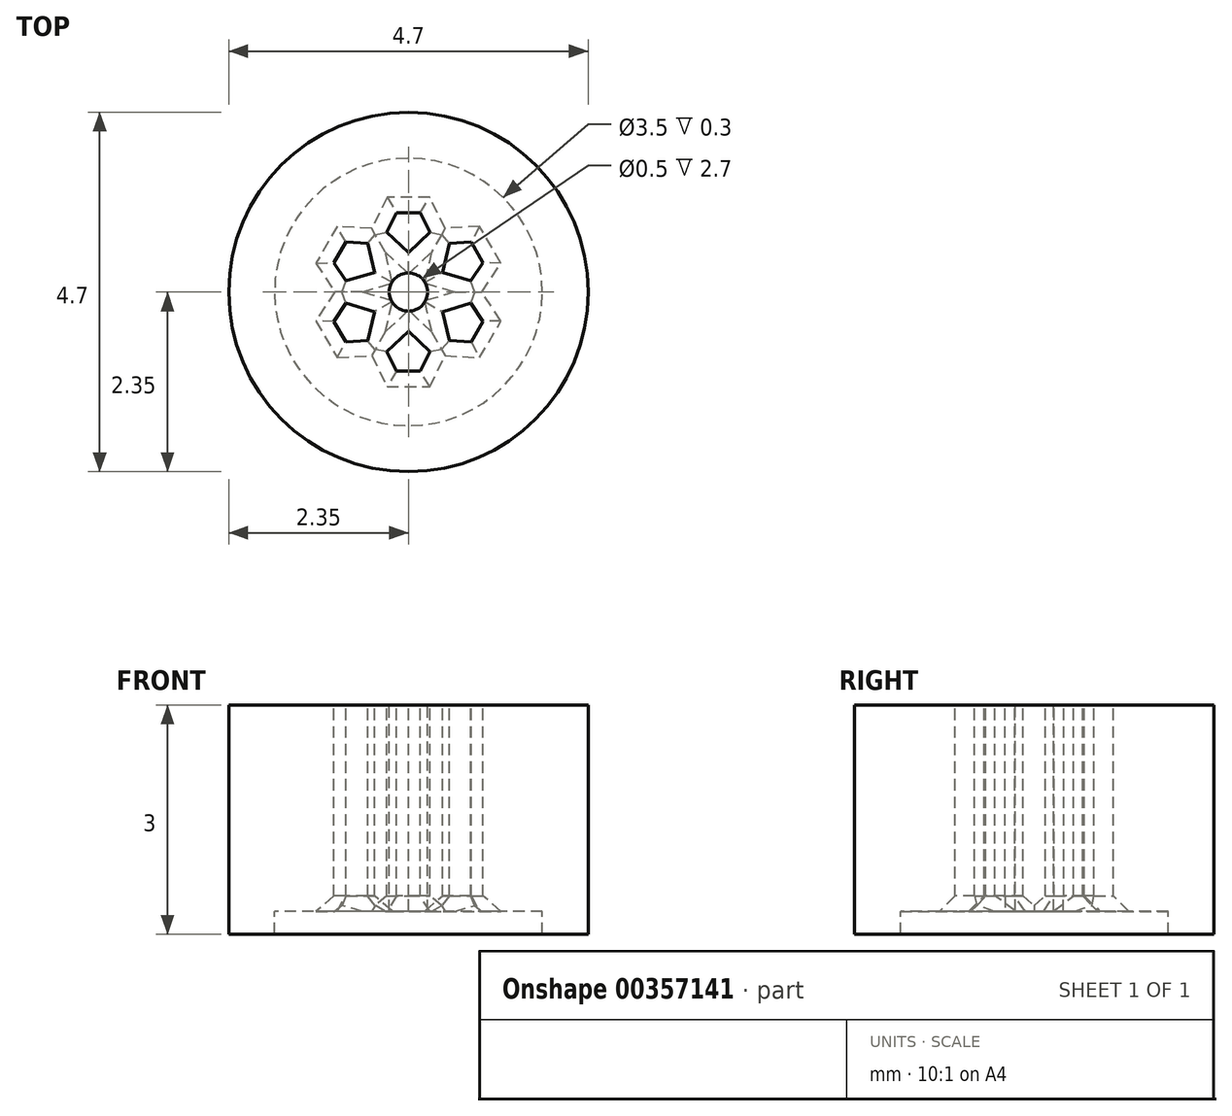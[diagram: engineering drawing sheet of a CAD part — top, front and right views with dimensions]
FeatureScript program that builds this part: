
annotation { "Feature Type Name" : "Feature", "Feature Type Description" : "" }
export const myFeature = defineFeature(function(context is Context, id is Id, definition is map)
    precondition{}
    {
        {
            var Q0;
            Q0=qCreatedBy(makeId("Top.planeOp"),FACE);
            var sketch = newSketch(context, id + "F0", { "sketchPlane" : qUnion([Q0])});
            skCircle(sketch, "E0", {"center": v(0, 0) * mm, "radius": 2.35 * mm});
            skCircle(sketch, "E1", {"center": v(0, 0) * mm, "radius": 1.75 * mm});
            skCircle(sketch, "E2", {"center": v(0, 0) * mm, "radius": 0.25 * mm});
            skLineSegment(sketch, "E3", {"start": v(0, 0.51) * mm, "end": v(0.28, 0.78) * mm});
            skLineSegment(sketch, "E4", {"start": v(0.28, 0.78) * mm, "end": v(0.15, 1.04) * mm});
            skLineSegment(sketch, "E5", {"start": v(0.15, 1.04) * mm, "end": v(0, 1.04) * mm});
            skLineSegment(sketch, "E6.MirrorCS", {"start": v(-0.15, 1.04) * mm, "end": v(0, 1.04) * mm});
            skLineSegment(sketch, "E7.MirrorCS", {"start": v(-0.28, 0.78) * mm, "end": v(-0.15, 1.04) * mm});
            skLineSegment(sketch, "E8.MirrorCS", {"start": v(0, 0.51) * mm, "end": v(-0.28, 0.78) * mm});
            skLineSegment(sketch, "E9.1.0", {"start": v(0.44, 0.26) * mm, "end": v(0.53, 0.63) * mm});
            skLineSegment(sketch, "E9.1.1", {"start": v(0.44, 0.26) * mm, "end": v(0.82, 0.14) * mm});
            skLineSegment(sketch, "E9.1.2", {"start": v(0.82, 0.14) * mm, "end": v(0.97, 0.38) * mm});
            skLineSegment(sketch, "E9.1.3", {"start": v(0.97, 0.38) * mm, "end": v(0.9, 0.52) * mm});
            skLineSegment(sketch, "E9.1.4", {"start": v(0.82, 0.65) * mm, "end": v(0.9, 0.52) * mm});
            skLineSegment(sketch, "E9.1.5", {"start": v(0.53, 0.63) * mm, "end": v(0.82, 0.65) * mm});
            skLineSegment(sketch, "E9.2.0", {"start": v(0.44, -0.26) * mm, "end": v(0.82, -0.14) * mm});
            skLineSegment(sketch, "E9.2.1", {"start": v(0.44, -0.26) * mm, "end": v(0.53, -0.63) * mm});
            skLineSegment(sketch, "E9.2.2", {"start": v(0.53, -0.63) * mm, "end": v(0.82, -0.65) * mm});
            skLineSegment(sketch, "E9.2.3", {"start": v(0.82, -0.65) * mm, "end": v(0.9, -0.52) * mm});
            skLineSegment(sketch, "E9.2.4", {"start": v(0.97, -0.38) * mm, "end": v(0.9, -0.52) * mm});
            skLineSegment(sketch, "E9.2.5", {"start": v(0.82, -0.14) * mm, "end": v(0.97, -0.38) * mm});
            skLineSegment(sketch, "E9.3.0", {"start": v(0, -0.51) * mm, "end": v(0.28, -0.78) * mm});
            skLineSegment(sketch, "E9.3.1", {"start": v(0, -0.51) * mm, "end": v(-0.28, -0.78) * mm});
            skLineSegment(sketch, "E9.3.2", {"start": v(-0.28, -0.78) * mm, "end": v(-0.15, -1.04) * mm});
            skLineSegment(sketch, "E9.3.3", {"start": v(-0.15, -1.04) * mm, "end": v(0, -1.04) * mm});
            skLineSegment(sketch, "E9.3.4", {"start": v(0.15, -1.04) * mm, "end": v(0, -1.04) * mm});
            skLineSegment(sketch, "E9.3.5", {"start": v(0.28, -0.78) * mm, "end": v(0.15, -1.04) * mm});
            skLineSegment(sketch, "E9.4.0", {"start": v(-0.44, -0.26) * mm, "end": v(-0.53, -0.63) * mm});
            skLineSegment(sketch, "E9.4.1", {"start": v(-0.44, -0.26) * mm, "end": v(-0.82, -0.14) * mm});
            skLineSegment(sketch, "E9.4.2", {"start": v(-0.82, -0.14) * mm, "end": v(-0.97, -0.38) * mm});
            skLineSegment(sketch, "E9.4.3", {"start": v(-0.97, -0.38) * mm, "end": v(-0.9, -0.52) * mm});
            skLineSegment(sketch, "E9.4.4", {"start": v(-0.82, -0.65) * mm, "end": v(-0.9, -0.52) * mm});
            skLineSegment(sketch, "E9.4.5", {"start": v(-0.53, -0.63) * mm, "end": v(-0.82, -0.65) * mm});
            skLineSegment(sketch, "E9.5.0", {"start": v(-0.44, 0.26) * mm, "end": v(-0.82, 0.14) * mm});
            skLineSegment(sketch, "E9.5.1", {"start": v(-0.44, 0.26) * mm, "end": v(-0.53, 0.63) * mm});
            skLineSegment(sketch, "E9.5.2", {"start": v(-0.53, 0.63) * mm, "end": v(-0.82, 0.65) * mm});
            skLineSegment(sketch, "E9.5.3", {"start": v(-0.82, 0.65) * mm, "end": v(-0.9, 0.52) * mm});
            skLineSegment(sketch, "E9.5.4", {"start": v(-0.97, 0.38) * mm, "end": v(-0.9, 0.52) * mm});
            skLineSegment(sketch, "E9.5.5", {"start": v(-0.82, 0.14) * mm, "end": v(-0.97, 0.38) * mm});
            skLineSegment(sketch, "E9.anchor1", {"start": v(0, 0) * mm, "end": v(-0.28, 0.78) * mm, "construction": true});
            skLineSegment(sketch, "E9.anchor2", {"start": v(0, 0) * mm, "end": v(-0.82, 0.14) * mm, "construction": true});
            skSolve(sketch);
        }
        {
            var Q0;
            Q0 = qSketchRegion(id + "F0", true);
            extrude(context, id + "F1", {"entities" : qUnion([Q0]), "oppositeDirection" : true, "depth" : 3 * mm});
        }
        {
            var Q0;
            Q0=makeQuery(id+"F0.imprint","IMPRINT",FACE,{"disambiguationData":[TD([[makeQuery(id+"F0.imprint","IMPRINT",EDGE,{"derivedFrom":sQuery(id+"F0.wireOp",EDGE,"E1")}),1.0]])]});
            extrude(context, id + "F2", {"entities" : qUnion([Q0]), "operationType" : NewBodyOperationType.ADD, "oppositeDirection" : true, "depth" : 2.7 * mm});
        }
        {
            var Q0;
            Q0=makeQuery(id+"F2.opExtrude","CAP_EDGE",EDGE,{"disambiguationData":[OSD([sQuery(id+"F0.wireOp",EDGE,"E9.5.1")])],"isStart":false});
            var Q1;
            Q1=makeQuery(id+"F2.opExtrude","CAP_EDGE",EDGE,{"disambiguationData":[OSD([sQuery(id+"F0.wireOp",EDGE,"E9.5.2")])],"isStart":false});
            var Q2;
            Q2=makeQuery(id+"F2.opExtrude","CAP_EDGE",EDGE,{"disambiguationData":[OSD([sQuery(id+"F0.wireOp",EDGE,"E9.5.3"),sQuery(id+"F0.wireOp",EDGE,"E9.5.4")])],"isStart":false});
            var Q3;
            Q3=makeQuery(id+"F2.opExtrude","CAP_EDGE",EDGE,{"disambiguationData":[OSD([sQuery(id+"F0.wireOp",EDGE,"E9.5.5")])],"isStart":false});
            var Q4;
            Q4=makeQuery(id+"F2.opExtrude","CAP_EDGE",EDGE,{"disambiguationData":[OSD([sQuery(id+"F0.wireOp",EDGE,"E9.5.0")])],"isStart":false});
            var Q5;
            Q5=makeQuery(id+"F2.opExtrude","CAP_EDGE",EDGE,{"disambiguationData":[OSD([sQuery(id+"F0.wireOp",EDGE,"E3")])],"isStart":false});
            var Q6;
            Q6=makeQuery(id+"F2.opExtrude","CAP_EDGE",EDGE,{"disambiguationData":[OSD([sQuery(id+"F0.wireOp",EDGE,"E4")])],"isStart":false});
            var Q7;
            Q7=makeQuery(id+"F2.opExtrude","CAP_EDGE",EDGE,{"disambiguationData":[OSD([sQuery(id+"F0.wireOp",EDGE,"E5"),sQuery(id+"F0.wireOp",EDGE,"E6.MirrorCS")])],"isStart":false});
            var Q8;
            Q8=makeQuery(id+"F2.opExtrude","CAP_EDGE",EDGE,{"disambiguationData":[OSD([sQuery(id+"F0.wireOp",EDGE,"E7.MirrorCS")])],"isStart":false});
            var Q9;
            Q9=makeQuery(id+"F2.opExtrude","CAP_EDGE",EDGE,{"disambiguationData":[OSD([sQuery(id+"F0.wireOp",EDGE,"E8.MirrorCS")])],"isStart":false});
            var Q10;
            Q10=makeQuery(id+"F2.opExtrude","CAP_EDGE",EDGE,{"disambiguationData":[OSD([sQuery(id+"F0.wireOp",EDGE,"E9.1.0")])],"isStart":false});
            var Q11;
            Q11=makeQuery(id+"F2.opExtrude","CAP_EDGE",EDGE,{"disambiguationData":[OSD([sQuery(id+"F0.wireOp",EDGE,"E9.1.5")])],"isStart":false});
            var Q12;
            Q12=makeQuery(id+"F2.opExtrude","CAP_EDGE",EDGE,{"disambiguationData":[OSD([sQuery(id+"F0.wireOp",EDGE,"E9.1.3"),sQuery(id+"F0.wireOp",EDGE,"E9.1.4")])],"isStart":false});
            var Q13;
            Q13=makeQuery(id+"F2.opExtrude","CAP_EDGE",EDGE,{"disambiguationData":[OSD([sQuery(id+"F0.wireOp",EDGE,"E9.1.2")])],"isStart":false});
            var Q14;
            Q14=makeQuery(id+"F2.opExtrude","CAP_EDGE",EDGE,{"disambiguationData":[OSD([sQuery(id+"F0.wireOp",EDGE,"E9.1.1")])],"isStart":false});
            var Q15;
            Q15=makeQuery(id+"F2.opExtrude","CAP_EDGE",EDGE,{"disambiguationData":[OSD([sQuery(id+"F0.wireOp",EDGE,"E9.2.1")])],"isStart":false});
            var Q16;
            Q16=makeQuery(id+"F2.opExtrude","CAP_EDGE",EDGE,{"disambiguationData":[OSD([sQuery(id+"F0.wireOp",EDGE,"E9.2.0")])],"isStart":false});
            var Q17;
            Q17=makeQuery(id+"F2.opExtrude","CAP_EDGE",EDGE,{"disambiguationData":[OSD([sQuery(id+"F0.wireOp",EDGE,"E9.2.5")])],"isStart":false});
            var Q18;
            Q18=makeQuery(id+"F2.opExtrude","CAP_EDGE",EDGE,{"disambiguationData":[OSD([sQuery(id+"F0.wireOp",EDGE,"E9.2.3"),sQuery(id+"F0.wireOp",EDGE,"E9.2.4")])],"isStart":false});
            var Q19;
            Q19=makeQuery(id+"F2.opExtrude","CAP_EDGE",EDGE,{"disambiguationData":[OSD([sQuery(id+"F0.wireOp",EDGE,"E9.2.2")])],"isStart":false});
            var Q20;
            Q20=makeQuery(id+"F2.opExtrude","CAP_EDGE",EDGE,{"disambiguationData":[OSD([sQuery(id+"F0.wireOp",EDGE,"E9.3.5")])],"isStart":false});
            var Q21;
            Q21=makeQuery(id+"F2.opExtrude","CAP_EDGE",EDGE,{"disambiguationData":[OSD([sQuery(id+"F0.wireOp",EDGE,"E9.3.0")])],"isStart":false});
            var Q22;
            Q22=makeQuery(id+"F2.opExtrude","CAP_EDGE",EDGE,{"disambiguationData":[OSD([sQuery(id+"F0.wireOp",EDGE,"E9.3.1")])],"isStart":false});
            var Q23;
            Q23=makeQuery(id+"F2.opExtrude","CAP_EDGE",EDGE,{"disambiguationData":[OSD([sQuery(id+"F0.wireOp",EDGE,"E9.3.2")])],"isStart":false});
            var Q24;
            Q24=makeQuery(id+"F2.opExtrude","CAP_EDGE",EDGE,{"disambiguationData":[OSD([sQuery(id+"F0.wireOp",EDGE,"E9.3.3"),sQuery(id+"F0.wireOp",EDGE,"E9.3.4")])],"isStart":false});
            var Q25;
            Q25=makeQuery(id+"F2.opExtrude","CAP_EDGE",EDGE,{"disambiguationData":[OSD([sQuery(id+"F0.wireOp",EDGE,"E9.4.5")])],"isStart":false});
            var Q26;
            Q26=makeQuery(id+"F2.opExtrude","CAP_EDGE",EDGE,{"disambiguationData":[OSD([sQuery(id+"F0.wireOp",EDGE,"E9.4.0")])],"isStart":false});
            var Q27;
            Q27=makeQuery(id+"F2.opExtrude","CAP_EDGE",EDGE,{"disambiguationData":[OSD([sQuery(id+"F0.wireOp",EDGE,"E9.4.1")])],"isStart":false});
            var Q28;
            Q28=makeQuery(id+"F2.opExtrude","CAP_EDGE",EDGE,{"disambiguationData":[OSD([sQuery(id+"F0.wireOp",EDGE,"E9.4.2")])],"isStart":false});
            var Q29;
            Q29=makeQuery(id+"F2.opExtrude","CAP_EDGE",EDGE,{"disambiguationData":[OSD([sQuery(id+"F0.wireOp",EDGE,"E9.4.3"),sQuery(id+"F0.wireOp",EDGE,"E9.4.4")])],"isStart":false});
            chamfer(context, id + "F3", {"entities" : qUnion([Q0, Q1, Q2, Q3, Q4, Q5, Q6, Q7, Q8, Q9, Q10, Q11, Q12, Q13, Q14, Q15, Q16, Q17, Q18, Q19, Q20, Q21, Q22, Q23, Q24, Q25, Q26, Q27, Q28, Q29]), "width" : .2 * mm, "tangentPropagation" : true});
        }
    });
